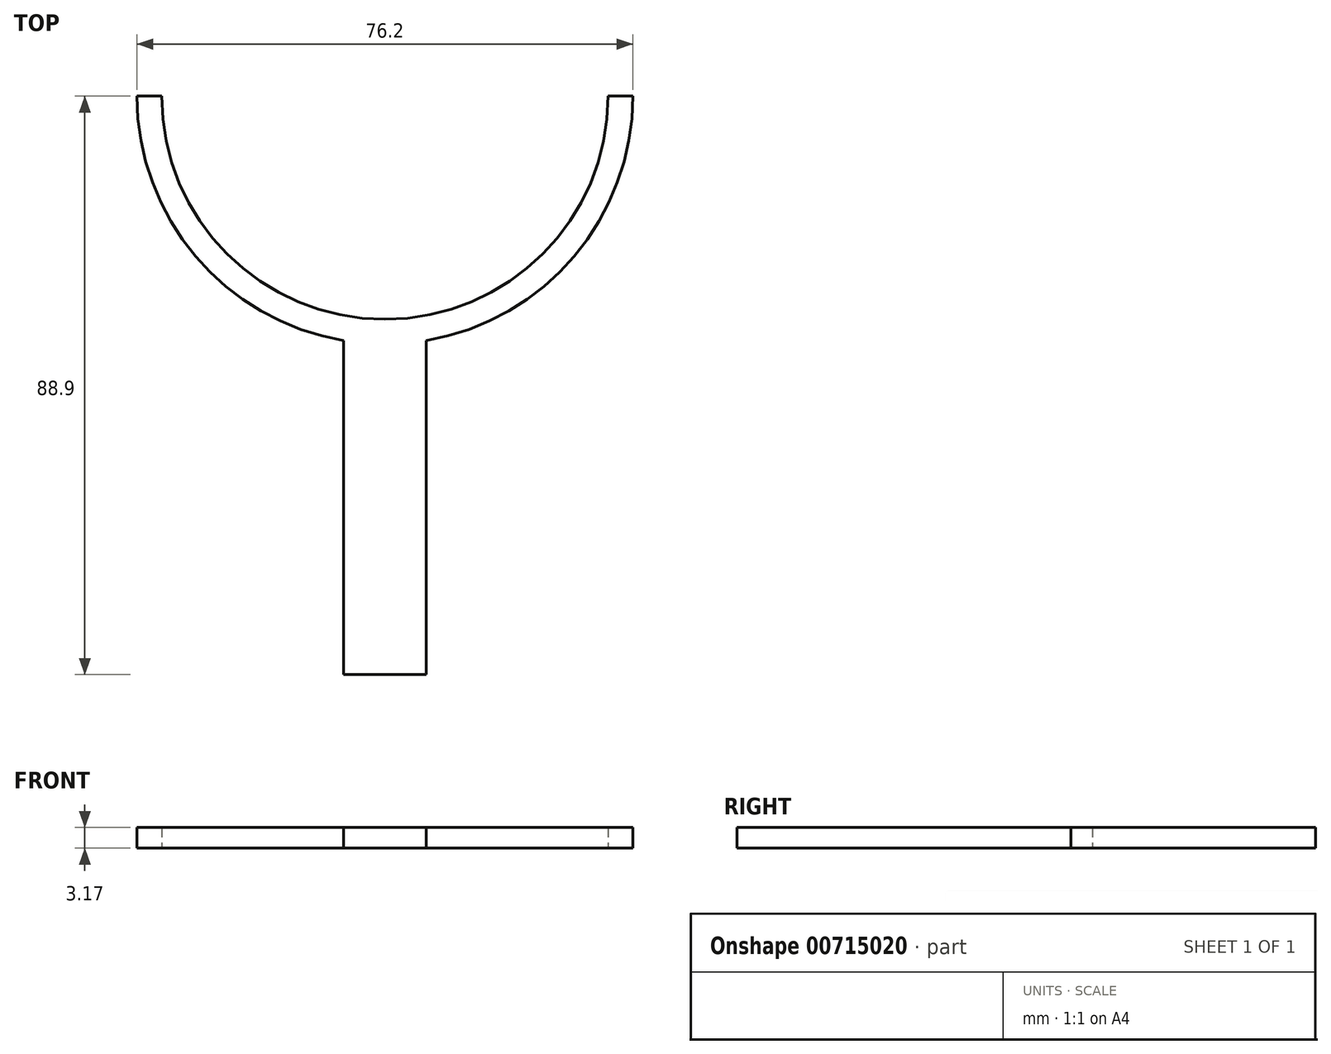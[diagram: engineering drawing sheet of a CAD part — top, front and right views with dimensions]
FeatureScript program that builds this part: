
annotation { "Feature Type Name" : "Feature", "Feature Type Description" : "" }
export const myFeature = defineFeature(function(context is Context, id is Id, definition is map)
    precondition{}
    {
        {
            var Q0;
            Q0=qCreatedBy(makeId("Top.planeOp"),FACE);
            var sketch = newSketch(context, id + "F0", { "sketchPlane" : qUnion([Q0])});
            skLineSegment(sketch, "E0.top", {"start": v(-6.35, -25.4) * mm, "end": v(6.35, -25.4) * mm});
            skLineSegment(sketch, "E0.left", {"start": v(-6.35, 25.4) * mm, "end": v(-6.35, -25.4) * mm});
            skLineSegment(sketch, "E0.right", {"start": v(6.35, 25.4) * mm, "end": v(6.35, -25.4) * mm});
            skPoint(sketch, "E0.middle", {"position": v(0, 0) * mm});
            skLineSegment(sketch, "E1", {"start": v(-6.35, 25.4) * mm, "end": v(-6.35, 25.93) * mm});
            skLineSegment(sketch, "E2", {"start": v(6.35, 25.4) * mm, "end": v(6.35, 25.93) * mm});
            skArc(sketch, "E3", {"start": v(-38.1, 63.5) * mm, "mid": v(0, 25.4) * mm, "end": v(38.1, 63.5) * mm});
            skArc(sketch, "E4", {"start": v(-34.3, 63.5) * mm, "mid": v(0, 29.2) * mm, "end": v(34.3, 63.5) * mm});
            skLineSegment(sketch, "E5", {"start": v(-34.3, 63.5) * mm, "end": v(-38.1, 63.5) * mm});
            skLineSegment(sketch, "E6", {"start": v(-38.1, 63.5) * mm, "end": v(-34.3, 63.5) * mm});
            skLineSegment(sketch, "E7.trimOffspring", {"start": v(34.3, 63.5) * mm, "end": v(38.1, 63.5) * mm});
            skPoint(sketch, "E8.start.orphan", {"position": v(0, 25.4) * mm});
            skSolve(sketch);
        }
        {
            var Q0;
            {var subQ1=sQuery(id+"F0.wireOp",EDGE,"Wwefo2Fw-wYnm-Wnqo-HFg0-P62vGOYn8pNC");Q0=makeQuery(id+"F0.imprint","IMPRINT",FACE,{"disambiguationData":[TD([[makeQuery(id+"F0.imprint","IMPRINT",EDGE,{"derivedFrom":subQ1}),-1.0]])]});}
            var Q1;
            Q1=makeQuery(id+"F0.imprint","IMPRINT",FACE,{"disambiguationData":[TD([[makeQuery(id+"F0.imprint","IMPRINT",EDGE,{"derivedFrom":sQuery(id+"F0.wireOp",EDGE,"E0.top")}),1.0]])]});
            var Q2;
            Q2=makeQuery(id+"F0.imprint","IMPRINT",FACE,{"disambiguationData":[TD([[makeQuery(id+"F0.imprint","IMPRINT",EDGE,{"derivedFrom":sQuery(id+"F0.wireOp",EDGE,"E4")}),-1.0]])]});
            extrude(context, id + "F1", {"entities" : qUnion([Q0, Q1, Q2]), "depth" : 3.17 * mm, "offsetDistance" : 25.4 * mm});
        }
    });
